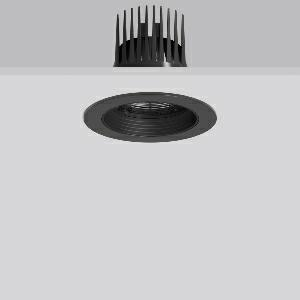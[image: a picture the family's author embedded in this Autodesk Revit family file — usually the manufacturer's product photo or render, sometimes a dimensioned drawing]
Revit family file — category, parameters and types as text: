
# Revit family: heledon_maxi_e_901767_003_2_76_8e1d
name_source: partatom
category: Lighting Fixtures
units: mm (PartAtom-declared; Revit-internal decimal feet)

## family parameters
Cut with Voids When Loaded = No
Host = Face
Light Source = No
Part Type = Normal
Room Calculation Point = No
Round Connector Dimension = Use Diameter
Shared = No

## types (1)
- HELEDON maxi E (1 x LED Modul 927, 3500 lm, 2700)
    Apparent Load = 35 VA
    Approval mark = CE
    CIE Flux Codes = 97 100 100 100 100
    Color Rendering = 92
    Color Temperature = 2700
    Default Elevation = 1800 mm
    Description = Series: HELEDON maxi
Round recessed downlight. Housing: die-cast aluminium, powder-coated. Black plastic ring and recessed LED to prevent glare from the side. Optical assembly with lens made of plastic (polycarbonate) for the best homogeneous light distribution - can be changed without tools. Best colour rendering index Ra>90. Suitable for Recessed ceiling mounting. Installation without tools thanks to spring fastening system. Including separate LED converter with connecting cable 600 mm.High quality converter without flickering and stroboscopic effect. Through-wiring box (5 pole) available as accessory. The following accessories can be mounted without use of tools: interchangeable lenses, decorative glasses, honeycomb louvre, clear and frosted diffusers, white interchangeable plastic ring. 
Colour: deep black, matt (RAL 9005)
Diameter: 162 mm
Height: 3 mm
Cut-out diameter: 152 mm
Recess height: 200 mm
Luminaire: recess height: 135 mm
Lamp: LED
Socket: without socket
Colour temperature: 2700K
Colour rendering index (CRI): 92
System power: 35 W
Rated luminous flux: 3500 lm
Luminous efficiency: 100 lm/W
Control gear: Converter, dimmable, DALI
Protection class: II
Type of protection: IP 20
    Height = 0 mm  [stored 0 ft]
    Lamp = 1 x LED Modul 927
    Lamp Light Flux = 3500 lm
    Lamp count = 1
    Length = 162 mm
    Lifetime = 50000 h
    Luminous efficacy = 100 lm/W
    Manufacturer = RZB
    ModVariant = No
    Model = 901767.003.2.76
    Mounting Place = Ceiling
    Mounting Type = Recessed
    Number of Poles = 1
    OnlyDefault = Yes
    Power Factor = 1
    Product Name = HELEDON maxi E
    Product group = Recessed downlights
    ProductGroupID = 402
    Protection Class = Protection class II
    Protection Degree = IP 20
    RLX_Detail_Level = 1
    RLX_Emergency_Light_Flux = 0 lm
    RLX_Emergency_Type = 0
    RLX_Emergency_Type_DB = No
    RlxData = <blob elided: 120677 chars, md5=ea80e1f4>
    Socket = socket
    Standby Power = 0 W
    System Light Flux = 3500 lm
    System Power = 35 W
    Type Comments = Product without accessories
    Type Image = 901663.003.jpg
    URL = http://relux.com
    VarID = ---
    Voltage = 230 V
    Voltage Range = 220-240 V
    Weight = 0.00 kg
    Width = 0 mm  [stored 0 ft]

note: [stored X ft] marks values corroborated as IEEE doubles in the binary element streams (Revit-internal decimal feet)

## geometry (parser evidence)
native form markers: Blend x4, Sweep x11
no freeform markers — native parametric forms only
